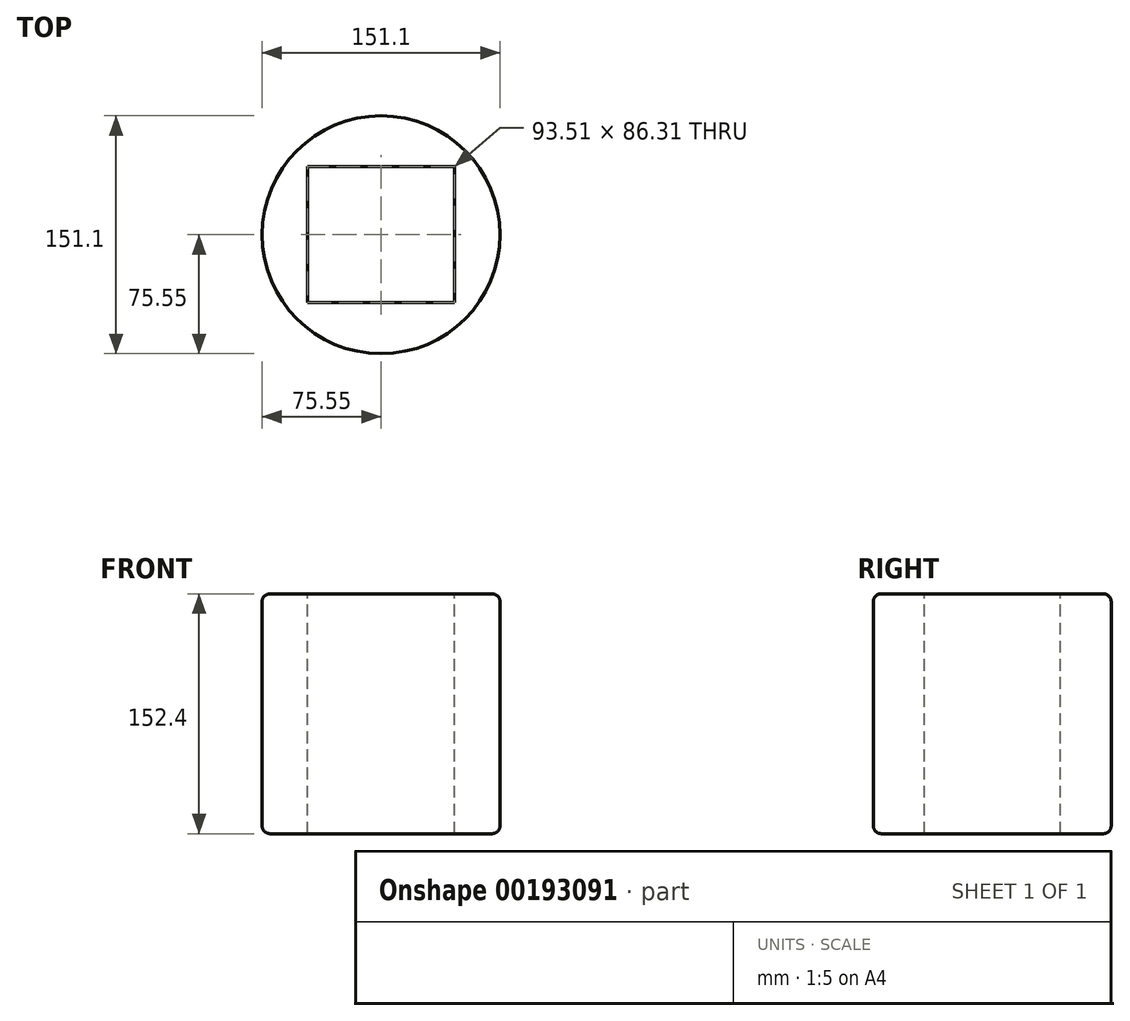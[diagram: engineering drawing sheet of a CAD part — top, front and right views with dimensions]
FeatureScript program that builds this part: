
annotation { "Feature Type Name" : "Feature", "Feature Type Description" : "" }
export const myFeature = defineFeature(function(context is Context, id is Id, definition is map)
    precondition{}
    {
        {
            var Q0;
            Q0=qCreatedBy(makeId("Top.planeOp"),FACE);
            var sketch = newSketch(context, id + "F0", { "sketchPlane" : qUnion([Q0])});
            skCircle(sketch, "E0", {"center": v(0, 0) * mm, "radius": 75.55 * mm});
            skSolve(sketch);
        }
        {
            var Q0;
            Q0=makeQuery(id+"F0.imprint","IMPRINT",FACE,{"disambiguationData":[TD([[makeQuery(id+"F0.imprint","IMPRINT",EDGE,{"derivedFrom":sQuery(id+"F0.wireOp",EDGE,"E0")}),1.0]])]});
            extrude(context, id + "F1", {"entities" : qUnion([Q0]), "depth" : 152.4 * mm});
        }
        {
            var Q0;
            Q0=makeQuery(id+"F1.opExtrude","CAP_FACE",FACE,{"disambiguationData":[OSD([sQuery(id+"F0.wireOp",EDGE,"E0")])],"isStart":false});
            fillet(context, id + "F2", {"entities" : qUnion([Q0]), "radius" : 5.08 * mm, "tangentPropagation" : true, "allowEdgeOverflow" : false});
        }
        {
            var Q0;
            Q0=makeQuery(id+"F1.opExtrude","CAP_FACE",FACE,{"disambiguationData":[OSD([sQuery(id+"F0.wireOp",EDGE,"E0")])],"isStart":false});
            var sketch = newSketch(context, id + "F3", { "sketchPlane" : qUnion([Q0])});
            skLineSegment(sketch, "E1.bottom", {"start": v(-46.76, 43.16) * mm, "end": v(46.76, 43.16) * mm});
            skLineSegment(sketch, "E1.top", {"start": v(-46.76, -43.16) * mm, "end": v(46.76, -43.16) * mm});
            skLineSegment(sketch, "E1.left", {"start": v(-46.76, 43.16) * mm, "end": v(-46.76, -43.16) * mm});
            skLineSegment(sketch, "E1.right", {"start": v(46.76, 43.16) * mm, "end": v(46.76, -43.16) * mm});
            skPoint(sketch, "E1.middle", {"position": v(0, 0) * mm});
            skSolve(sketch);
        }
        {
            var Q0;
            Q0=makeQuery(id+"F3.imprint","IMPRINT",FACE,{"disambiguationData":[TD([[makeQuery(id+"F3.imprint","IMPRINT",EDGE,{"derivedFrom":sQuery(id+"F3.wireOp",EDGE,"E1.bottom")}),-1.0]])]});
            extrude(context, id + "F4", {"entities" : qUnion([Q0]), "operationType" : NewBodyOperationType.REMOVE, "oppositeDirection" : true, "depth" : 152.4 * mm});
        }
        {
            var Q0;
            Q0=makeQuery(id+"F1.opExtrude","CAP_EDGE",EDGE,{"disambiguationData":[OSD([sQuery(id+"F0.wireOp",EDGE,"E0")])],"isStart":true});
            fillet(context, id + "F5", {"entities" : qUnion([Q0]), "radius" : 5.08 * mm, "tangentPropagation" : true, "allowEdgeOverflow" : false});
        }
    });
